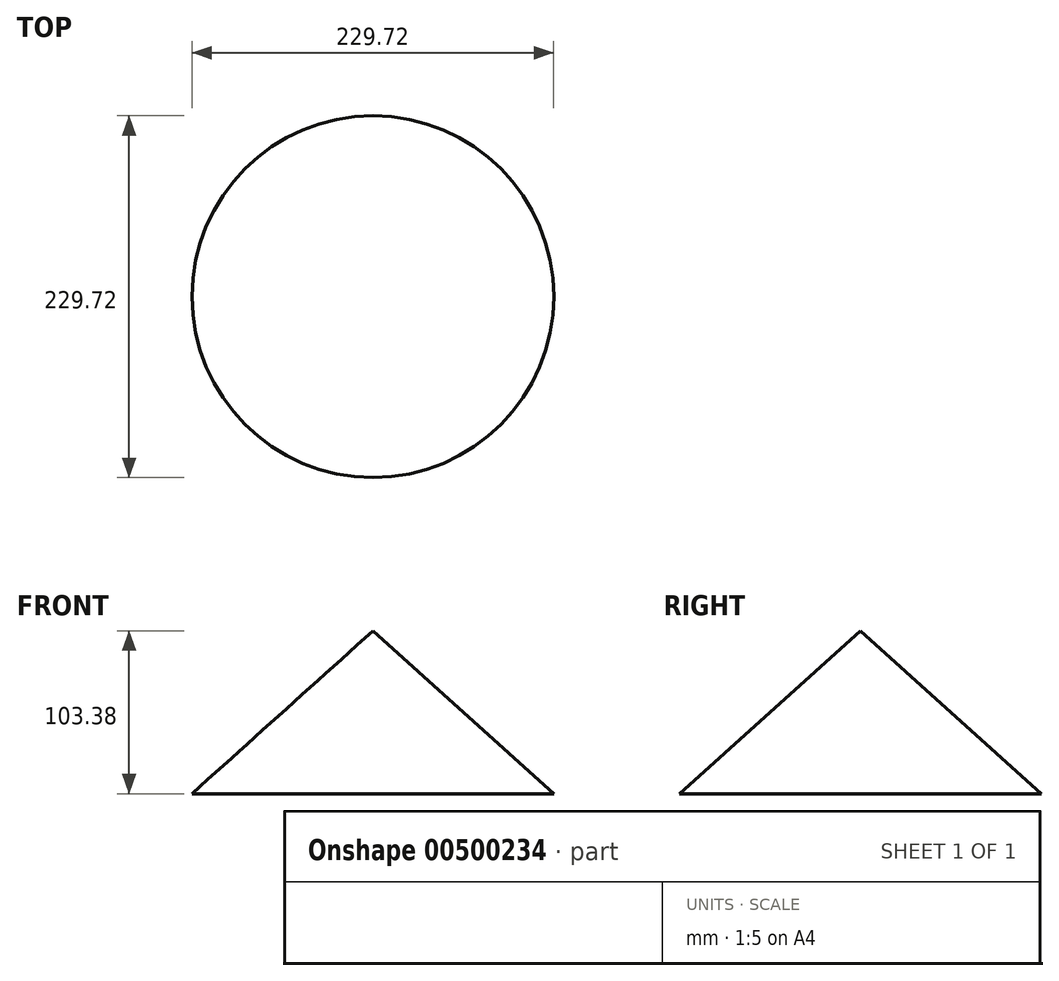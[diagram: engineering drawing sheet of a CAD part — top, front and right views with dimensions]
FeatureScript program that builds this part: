
annotation { "Feature Type Name" : "Feature", "Feature Type Description" : "" }
export const myFeature = defineFeature(function(context is Context, id is Id, definition is map)
    precondition{}
    {
        {
            var Q0;
            Q0=qCreatedBy(makeId("Top.planeOp"),FACE);
            var sketch = newSketch(context, id + "F0", { "sketchPlane" : qUnion([Q0])});
            skCircle(sketch, "E0", {"center": v(0, 0) * mm, "radius": 114.86 * mm});
            skSolve(sketch);
        }
        {
            var Q0;
            Q0=qCreatedBy(makeId("Top.planeOp"),FACE);
            cPlane(context, id + "F1", {"entities" : qUnion([Q0]), "cplaneType" : CPlaneType.OFFSET, "offset" : 103.38 * mm, "width" : 152.4 * mm, "height" : 152.4 * mm});
        }
        {
            var Q0;
            Q0=qCreatedBy(id+"F1.planeOp",FACE);
            var sketch = newSketch(context, id + "F2", { "sketchPlane" : qUnion([Q0])});
            skPoint(sketch, "E1", {"position": v(0, 0) * mm});
            skSolve(sketch);
        }
        {
            var Q0;
            Q0=sQuery(id+"F2.wireOp",VERTEX,"E1");
            var Q1;
            Q1=makeQuery(id+"F0.imprint","IMPRINT",FACE,{"disambiguationData":[TD([[makeQuery(id+"F0.imprint","IMPRINT",EDGE,{"derivedFrom":sQuery(id+"F0.wireOp",EDGE,"E0")}),1.0]])]});
            loft(context, id + "F3", {"sheetProfilesArray" : [{ "sheetProfileEntities" : qUnion([Q0]) }, { "sheetProfileEntities" : qUnion([Q1]) }]});
        }
    });
